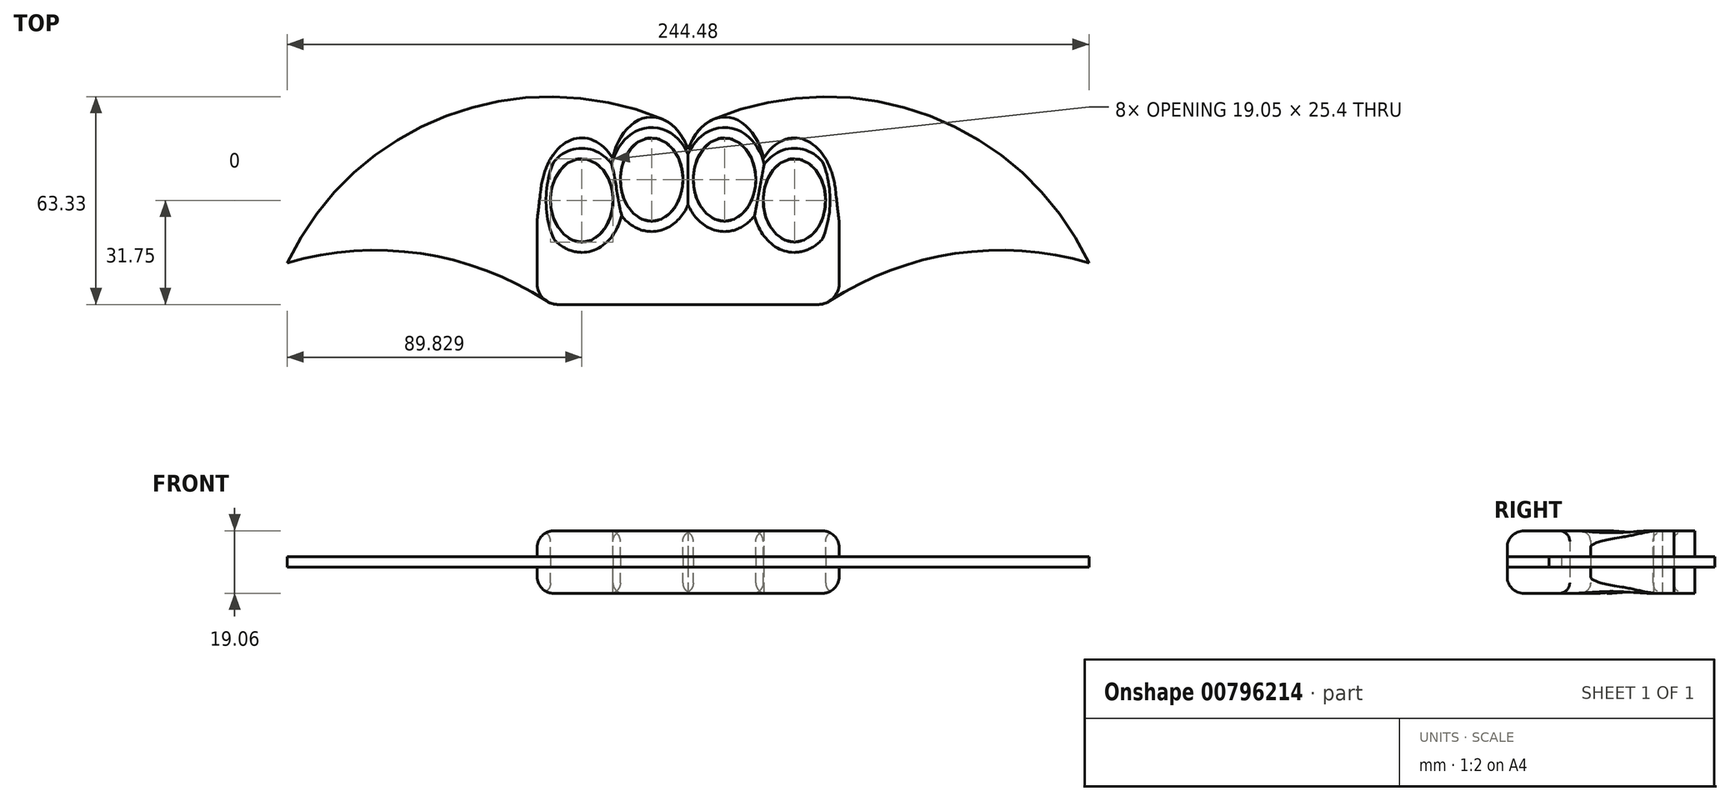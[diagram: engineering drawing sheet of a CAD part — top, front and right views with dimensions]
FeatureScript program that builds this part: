
annotation { "Feature Type Name" : "Feature", "Feature Type Description" : "" }
export const myFeature = defineFeature(function(context is Context, id is Id, definition is map)
    precondition{}
    {
        {
            var Q0;
            Q0=qCreatedBy(makeId("Top.planeOp"),FACE);
            var sketch = newSketch(context, id + "F0", { "sketchPlane" : qUnion([Q0])});
            skLineSegment(sketch, "E0.bottom", {"start": v(39.69, -12.7) * mm, "end": v(-39.69, -12.7) * mm});
            skLineSegment(sketch, "E0.left", {"start": v(46.04, -6.35) * mm, "end": v(46.04, 12.7) * mm});
            skLineSegment(sketch, "E0.right", {"start": v(-46.04, -6.35) * mm, "end": v(-46.04, 12.7) * mm});
            skPoint(sketch, "E0.middle", {"position": v(0, 0) * mm});
            skEllipse(sketch, "E1", {"center": v(-11.11, 25.4) * mm, "majorRadius": 12.7 * mm, "minorRadius": 9.53 * mm, "majorAxis": v(0, -1)});
            skPoint(sketch, "E2", {"position": v(-1.59, 25.4) * mm});
            skPoint(sketch, "E3", {"position": v(-11.11, 12.7) * mm});
            skEllipse(sketch, "E4", {"center": v(-32.41, 19.05) * mm, "majorRadius": 12.7 * mm, "minorRadius": 9.53 * mm, "majorAxis": v(0, -1)});
            skPoint(sketch, "E5", {"position": v(-32.41, 6.35) * mm});
            skEllipticalArc(sketch, "E6", {});
            skLineSegment(sketch, "E7", {"start": v(-46.04, 12.7) * mm, "end": v(-44.92, 22.31) * mm});
            skPoint(sketch, "E8.visualSharp", {"position": v(-46.04, -12.7) * mm});
            skArc(sketch, "E8.filletArc", {"start": v(-46.04, -6.35) * mm, "mid": v(-44.18, -10.84) * mm, "end": v(-39.69, -12.7) * mm});
            skPoint(sketch, "E9.visualSharp", {"position": v(46.04, -12.7) * mm});
            skArc(sketch, "E9.filletArc", {"start": v(39.69, -12.7) * mm, "mid": v(44.18, -10.84) * mm, "end": v(46.04, -6.35) * mm});
            skLineSegment(sketch, "E10", {"start": v(0, 83.87) * mm, "end": v(0, -58.38) * mm, "construction": true});
            skEllipse(sketch, "E11.MirrorC", {"center": v(11.11, 25.4) * mm, "majorRadius": 12.7 * mm, "minorRadius": 9.53 * mm, "majorAxis": v(0, -1)});
            skEllipticalArc(sketch, "E12.MirrorC", {});
            skEllipse(sketch, "E13.MirrorC", {"center": v(32.41, 19.05) * mm, "majorRadius": 12.7 * mm, "minorRadius": 9.53 * mm, "majorAxis": v(0, -1)});
            skLineSegment(sketch, "E14.MirrorCS", {"start": v(46.04, 12.7) * mm, "end": v(44.92, 22.31) * mm});
            skEllipticalArc(sketch, "E15.trimOffspring", {});
            skEllipticalArc(sketch, "E16.trimOffspring", {});
            skPoint(sketch, "E17", {"position": v(-11.11, 44.45) * mm});
            skPoint(sketch, "E18", {"position": v(11.11, 44.45) * mm});
            skPoint(sketch, "E19", {"position": v(36.48, 37.1) * mm});
            const initialGuessF0  = {"E6": [-0.03241104748568551, 0.01905, 0, -1, 0.01905, 0.0127, 2.3123841252391624, 4.54026013451959], "E12.MirrorC": [0.03241104748568551, 0.01905, 0, -1, 0.01905, 0.0127, 1.7429251726599961, 3.9708011819404234], "E15.trimOffspring": [-0.011112500000000006, 0.0254, 0, -1, 0.01905, 0.0127, 2.076156837079053, 4.363210193149401], "E16.trimOffspring": [0.011112500000000006, 0.0254, 0, -1, 0.01905, 0.0127, 1.9199751140301844, 4.207028470100534]};
            skSetInitialGuess(sketch, initialGuessF0);
            skSolve(sketch);
        }
        {
            var Q0;
            Q0 = qSketchRegion(id + "F0", true);
            extrude(context, id + "F1", {"entities" : qUnion([Q0]), "depth" : 9.52 * mm, "offsetDistance" : 25.4 * mm, "hasSecondDirection" : true, "secondDirectionOppositeDirection" : true, "secondDirectionDepth" : 9.52 * mm});
        }
        {
            var Q0;
            Q0=makeQuery(id+"F1.opExtrude","CAP_EDGE",EDGE,{"disambiguationData":[OSD([sQuery(id+"F0.wireOp",EDGE,"E11.MirrorC")])],"isStart":false});
            var Q1;
            Q1=makeQuery(id+"F1.opExtrude","CAP_EDGE",EDGE,{"disambiguationData":[OSD([sQuery(id+"F0.wireOp",EDGE,"E1")])],"isStart":false});
            var Q2;
            Q2=makeQuery(id+"F1.opExtrude","CAP_EDGE",EDGE,{"disambiguationData":[OSD([sQuery(id+"F0.wireOp",EDGE,"E4")])],"isStart":false});
            var Q3;
            Q3=makeQuery(id+"F1.opExtrude","CAP_EDGE",EDGE,{"disambiguationData":[OSD([sQuery(id+"F0.wireOp",EDGE,"E13.MirrorC")])],"isStart":false});
            var Q4;
            Q4=makeQuery(id+"F1.opExtrude","CAP_EDGE",EDGE,{"disambiguationData":[OSD([sQuery(id+"F0.wireOp",EDGE,"E1")])],"isStart":true});
            var Q5;
            Q5=makeQuery(id+"F1.opExtrude","CAP_EDGE",EDGE,{"disambiguationData":[OSD([sQuery(id+"F0.wireOp",EDGE,"E4")])],"isStart":true});
            var Q6;
            Q6=makeQuery(id+"F1.opExtrude","CAP_EDGE",EDGE,{"disambiguationData":[OSD([sQuery(id+"F0.wireOp",EDGE,"E11.MirrorC")])],"isStart":true});
            var Q7;
            Q7=makeQuery(id+"F1.opExtrude","CAP_EDGE",EDGE,{"disambiguationData":[OSD([sQuery(id+"F0.wireOp",EDGE,"E13.MirrorC")])],"isStart":true});
            fillet(context, id + "F2", {"entities" : qUnion([Q0, Q1, Q2, Q3, Q4, Q5, Q6, Q7]), "radius" : 3.17 * mm, "tangentPropagation" : true, "allowEdgeOverflow" : false});
        }
        {
            var Q0;
            Q0=qCreatedBy(makeId("Top.planeOp"),FACE);
            var sketch = newSketch(context, id + "F3", { "sketchPlane" : qUnion([Q0])});
            skEllipse(sketch, "E20", {"center": v(-11.11, 25.4) * mm, "majorRadius": 12.7 * mm, "minorRadius": 9.53 * mm, "majorAxis": v(0, -1)});
            skEllipse(sketch, "E21", {"center": v(-32.41, 19.05) * mm, "majorRadius": 12.7 * mm, "minorRadius": 9.53 * mm, "majorAxis": v(0, -1)});
            skEllipticalArc(sketch, "E22", {});
            skPoint(sketch, "E23", {"position": v(-122.24, 0) * mm});
            skArc(sketch, "E24", {"start": v(-7.7, 43.75) * mm, "mid": v(-73.72, 44.78) * mm, "end": v(-122.24, 0) * mm});
            skArc(sketch, "E25", {"start": v(-43.15, -11.67) * mm, "mid": v(-81.42, 2.8) * mm, "end": v(-122.24, 0) * mm});
            skPoint(sketch, "E26", {"position": v(0, 34.62) * mm});
            skArc(sketch, "E27", {"start": v(-39.69, -12.7) * mm, "mid": v(-44.18, -10.84) * mm, "end": v(-46.04, -6.35) * mm});
            skLineSegment(sketch, "E28", {"start": v(-39.69, -12.7) * mm, "end": v(0, -12.7) * mm});
            skLineSegment(sketch, "E29.MirrorCS", {"start": v(39.69, -12.7) * mm, "end": v(0, -12.7) * mm});
            skArc(sketch, "E30.MirrorCS", {"start": v(39.69, -12.7) * mm, "mid": v(44.18, -10.84) * mm, "end": v(46.04, -6.35) * mm});
            skArc(sketch, "E31.MirrorCS", {"start": v(43.15, -11.67) * mm, "mid": v(81.42, 2.8) * mm, "end": v(122.24, 0) * mm});
            skArc(sketch, "E32.MirrorCS", {"start": v(7.7, 43.75) * mm, "mid": v(73.72, 44.78) * mm, "end": v(122.24, 0) * mm});
            skEllipse(sketch, "E33.MirrorC", {"center": v(32.41, 19.05) * mm, "majorRadius": 12.7 * mm, "minorRadius": 9.53 * mm, "majorAxis": v(0, -1)});
            skEllipse(sketch, "E34.MirrorC", {"center": v(11.11, 25.4) * mm, "majorRadius": 12.7 * mm, "minorRadius": 9.53 * mm, "majorAxis": v(0, -1)});
            skEllipticalArc(sketch, "E35.MirrorCS", {});
            const initialGuessF3  = {"E22": [-0.011112500000000006, 0.0254, 0, -1, 0.01905, 0.0127, 2.076156837079053, 2.8697495965098425], "E35.MirrorCS": [0.011112500000000006, 0.0254, 0, -1, 0.01905, 0.0127, 3.4134357106697437, 4.207028470100534]};
            skSetInitialGuess(sketch, initialGuessF3);
            skSolve(sketch);
        }
        {
            var Q0;
            Q0=makeQuery(id+"F3.imprint","IMPRINT",FACE,{"disambiguationData":[TD([[makeQuery(id+"F3.imprint","IMPRINT",EDGE,{"derivedFrom":sQuery(id+"F3.wireOp",EDGE,"E20")}),-1.0]])]});
            extrude(context, id + "F4", {"entities" : qUnion([Q0]), "operationType" : NewBodyOperationType.REMOVE, "oppositeDirection" : true, "depth" : 1.59 * mm, "offsetDistance" : 25.4 * mm, "hasSecondDirection" : true, "secondDirectionOppositeDirection" : false, "secondDirectionDepth" : 1.59 * mm});
        }
        {
            var Q0;
            Q0=makeQuery(id+"F3.imprint","IMPRINT",FACE,{"disambiguationData":[TD([[makeQuery(id+"F3.imprint","IMPRINT",EDGE,{"derivedFrom":sQuery(id+"F3.wireOp",EDGE,"E20")}),-1.0]])]});
            extrude(context, id + "F5", {"entities" : qUnion([Q0]), "depth" : 1.59 * mm, "offsetDistance" : 25.4 * mm, "hasSecondDirection" : true, "secondDirectionOppositeDirection" : true, "secondDirectionDepth" : 1.59 * mm});
        }
        {
            var Q0;
            Q0=makeQuery(id+"F1.opExtrude","CAP_EDGE",EDGE,{"disambiguationData":[OSD([sQuery(id+"F0.wireOp",EDGE,"E0.bottom")])],"isStart":false});
            var Q1;
            Q1=makeQuery(id+"F1.opExtrude","CAP_EDGE",EDGE,{"disambiguationData":[OSD([sQuery(id+"F0.wireOp",EDGE,"E0.bottom")])],"isStart":true});
            fillet(context, id + "F6", {"entities" : qUnion([Q0, Q1]), "radius" : 5.08 * mm, "tangentPropagation" : true, "allowEdgeOverflow" : false});
        }
    });
